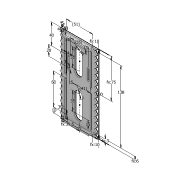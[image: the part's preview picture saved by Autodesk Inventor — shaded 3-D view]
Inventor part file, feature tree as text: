
AUTODESK INVENTOR PART (.ipt)
format: ipt  version: 2022 (Build 260153000, 153)  size: 247,808 bytes
history: native  units: mm
features: extrude x4, sketch x1, fillet x1
ambient origin geometry x8: Origin, YZ Plane, XZ Plane, XY Plane, X Axis, Y Axis, Z Axis, Center Point
bodies: Solid1 (feature_tree)
feature tree (6):
  sketch  "Sketch1"  dims[d0=71.0mm d1=150.0mm d2=45.0deg d3=5.0mm d4=150.0mm d6=10.0mm d7=10.0mm d9=10.0mm d11=35.5mm d12=10.0mm d13=10.0mm d14=3.0mm d15=10.0mm d16=3.0mm d17=138.0mm d19=6.0mm d20=3.2mm d21=11.0mm d22=10.0mm d24=51.0mm d25=3.0mm d26=4.0mm d27=40.0mm d28=20.0mm d29=35.0mm d30=41.0mm d31=2.5mm d32=0.0mm d33=8.0mm d34=0.0mm d35=3.0mm d36=35.0mm d37=15.0mm d38=15.0mm d39=35.0mm d40=15.0mm d41=15.0mm d42=0.0mm d43=0.0mm d44=60.0mm d45=75.0mm d46=0.0mm d47=0.0mm]
  extrude  "Extrusion1"  Depth=150.0mm
  extrude  "Extrusion2"  TaperAngle=45.0deg  [1 undecoded]
  fillet  "Fillet1"  Radius=5.0mm
  extrude  "Extrusion3"  Depth=150.0mm
  extrude  "Extrusion4"  Depth=60.0mm
note: 1 required parameter value undecoded (feature->parameter linkage not recoverable at this tier; creation-order binding heuristic only, values carry confidence <= 0.55)
